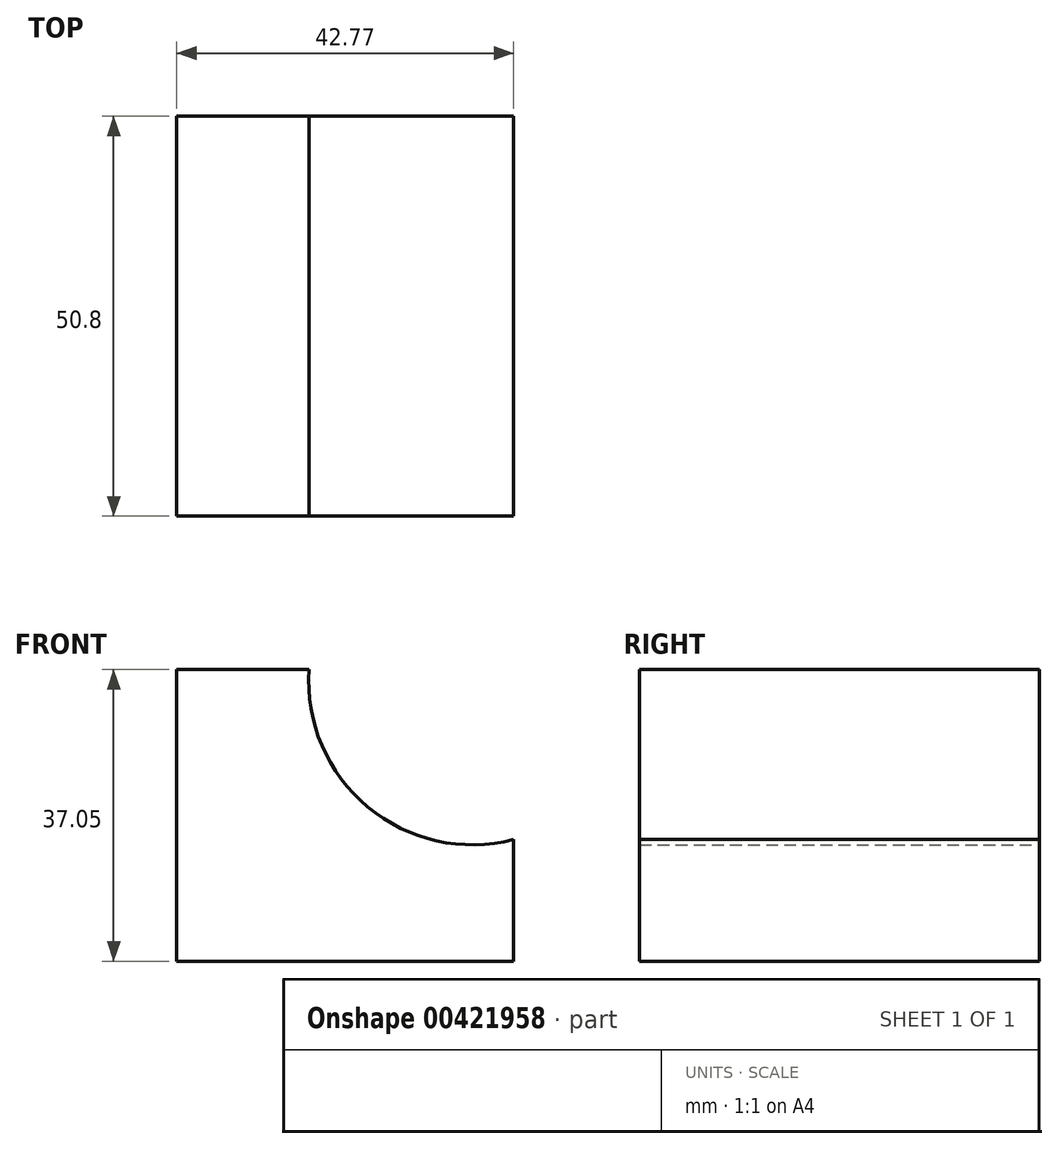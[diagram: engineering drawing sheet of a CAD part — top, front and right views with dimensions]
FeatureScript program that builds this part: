
annotation { "Feature Type Name" : "Feature", "Feature Type Description" : "" }
export const myFeature = defineFeature(function(context is Context, id is Id, definition is map)
    precondition{}
    {
        {
            var Q0;
            Q0=qCreatedBy(makeId("Front.planeOp"),FACE);
            var sketch = newSketch(context, id + "F0", { "sketchPlane" : qUnion([Q0])});
            skLineSegment(sketch, "E0", {"start": v(0, 0) * mm, "end": v(-42.77, 0) * mm});
            skLineSegment(sketch, "E1", {"start": v(-42.77, 0) * mm, "end": v(-42.77, 37.05) * mm});
            skLineSegment(sketch, "E2", {"start": v(-42.77, 37.05) * mm, "end": v(-25.97, 37.05) * mm});
            skLineSegment(sketch, "E3", {"start": v(0, 15.47) * mm, "end": v(0, 0) * mm});
            skArc(sketch, "E4", {"start": v(-25.97, 37.05) * mm, "mid": v(-18.52, 19.6) * mm, "end": v(0, 15.47) * mm});
            skSolve(sketch);
        }
        {
            var Q0;
            Q0=makeQuery(id+"F0.imprint","IMPRINT",FACE,{"disambiguationData":[TD([[makeQuery(id+"F0.imprint","IMPRINT",EDGE,{"derivedFrom":sQuery(id+"F0.wireOp",EDGE,"E0")}),-1.0]])]});
            extrude(context, id + "F1", {"entities" : qUnion([Q0]), "depth" : 50.8 * mm});
        }
    });
